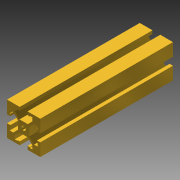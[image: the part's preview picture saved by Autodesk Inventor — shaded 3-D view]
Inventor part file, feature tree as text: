
AUTODESK INVENTOR PART (.ipt)
format: ipt  version: 2014 (Build 180170000, 170)  size: 152,064 bytes
history: native  units: in
note: dims shown in document units (in); Inventor stores cm internally (conversion verified against a paired STEP export)
features: extrude x2, plane x2, sketch x2, pattern_circular x1
ambient origin geometry x8: Origin, YZ Plane, XZ Plane, XY Plane, X Axis, Y Axis, Z Axis, Center Point
bodies: Solid1 (feature_tree)
feature tree (7):
  extrude  "Extrusion1"  Depth=0.515in
  extrude  "Extrusion2"  TaperAngle=45.0deg  [1 undecoded]
  pattern_circular  "Circular Pattern1"  [2 undecoded]
  plane  "Work Plane1"
  plane  "Work Plane2"
  sketch  "Sketch1"  dims[d0=0.515in d1=0.19in]
  sketch  "Sketch2"  dims[d2=6.0in d3=0.0in d5=45.0deg d6=0.575in d7=0.15in d8=0.12in d9=0.75in d10=0.75in d13=0.35in d14=0.05in d15=0.125in d16=1.0in d17=0.0in d18=1.5748in d19=360.0deg d21=0.0in d22=0.0in]
note: 3 required parameter values undecoded (feature->parameter linkage not recoverable at this tier; creation-order binding heuristic only, values carry confidence <= 0.55)
